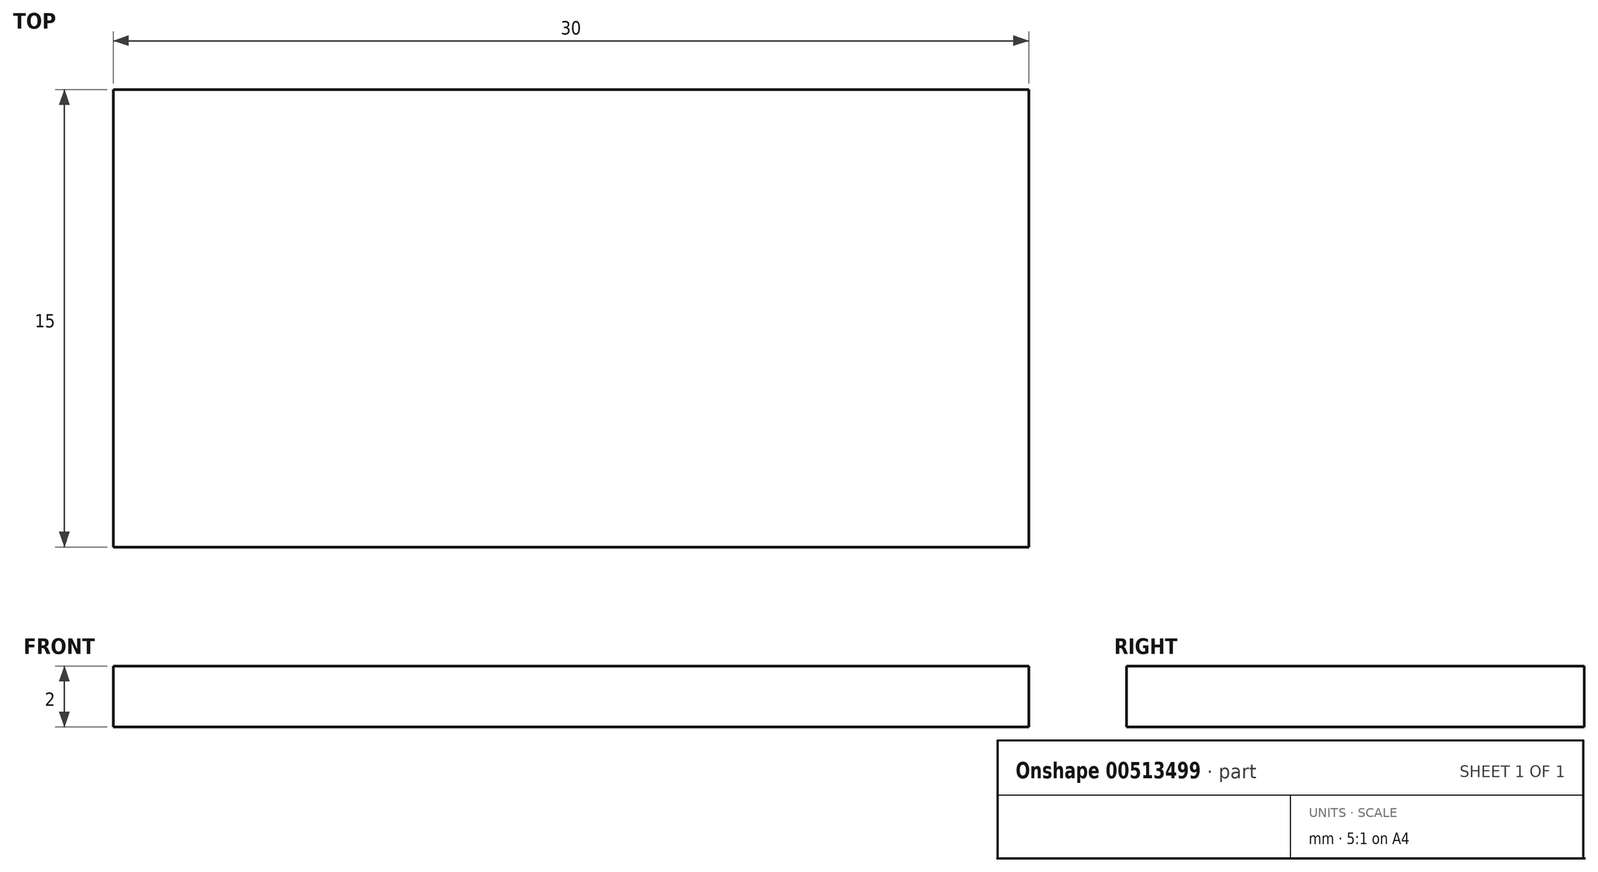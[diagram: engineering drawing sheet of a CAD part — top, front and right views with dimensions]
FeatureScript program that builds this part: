
annotation { "Feature Type Name" : "Feature", "Feature Type Description" : "" }
export const myFeature = defineFeature(function(context is Context, id is Id, definition is map)
    precondition{}
    {
        {
            var Q0;
            Q0=qCreatedBy(makeId("Top.planeOp"),FACE);
            var sketch = newSketch(context, id + "F0", { "sketchPlane" : qUnion([Q0])});
            skLineSegment(sketch, "E0.bottom", {"start": v(15, -7.5) * mm, "end": v(-15, -7.5) * mm});
            skLineSegment(sketch, "E0.top", {"start": v(15, 7.5) * mm, "end": v(-15, 7.5) * mm});
            skLineSegment(sketch, "E0.left", {"start": v(15, -7.5) * mm, "end": v(15, 7.5) * mm});
            skLineSegment(sketch, "E0.right", {"start": v(-15, -7.5) * mm, "end": v(-15, 7.5) * mm});
            skPoint(sketch, "E0.middle", {"position": v(0, 0) * mm});
            skSolve(sketch);
        }
        {
            var Q0;
            Q0=makeQuery(id+"F0.imprint","IMPRINT",FACE,{"disambiguationData":[TD([[makeQuery(id+"F0.imprint","IMPRINT",EDGE,{"derivedFrom":sQuery(id+"F0.wireOp",EDGE,"E0.bottom")}),-1.0]])]});
            extrude(context, id + "F1", {"entities" : qUnion([Q0]), "depth" : 2 * mm});
        }
    });
